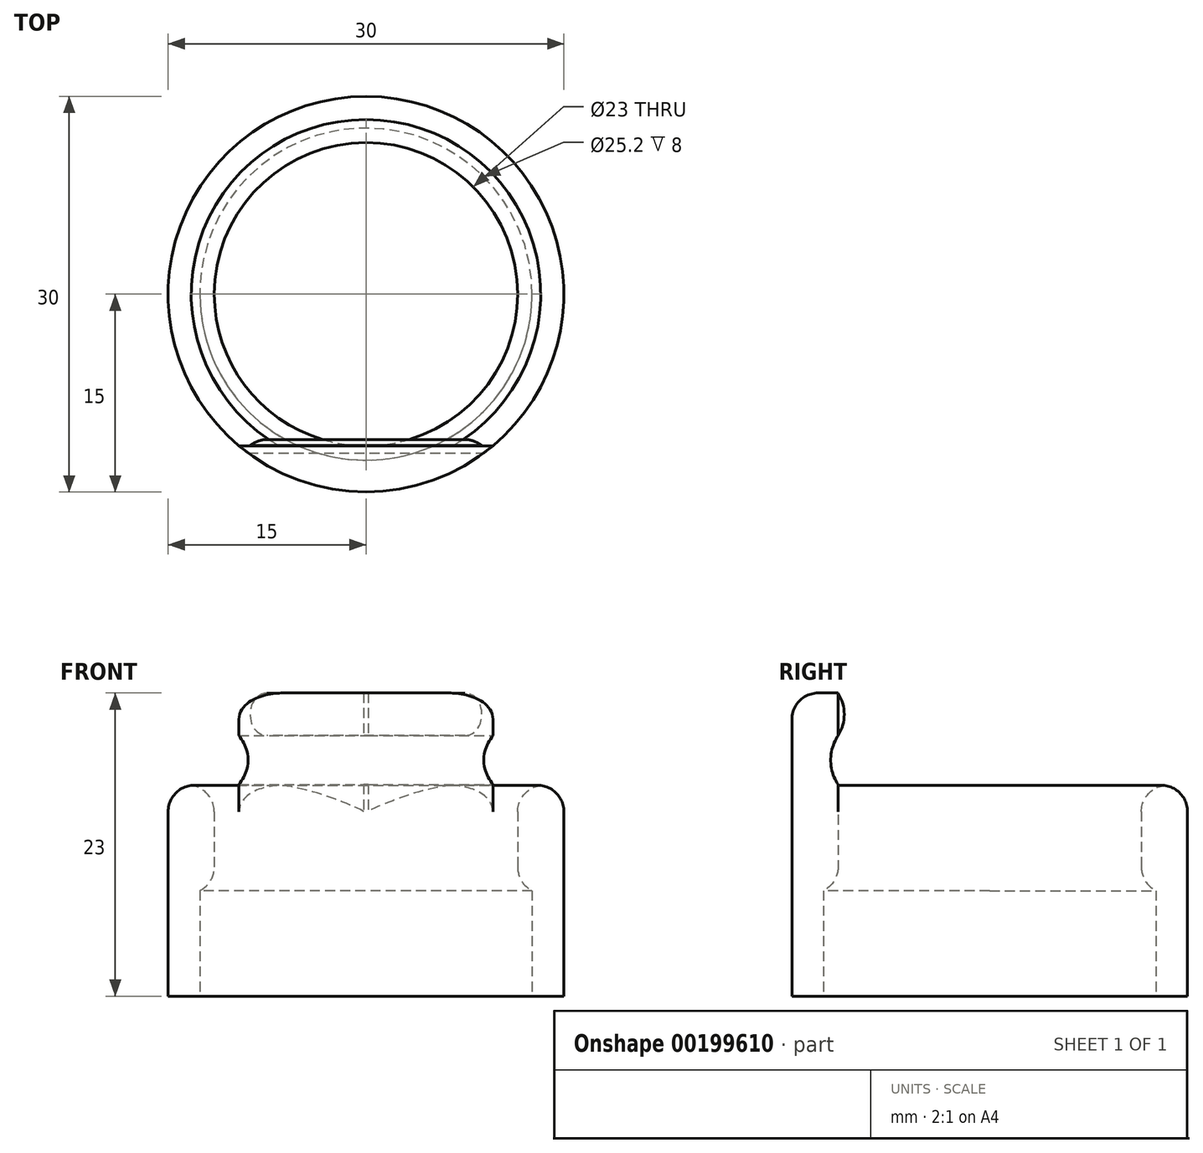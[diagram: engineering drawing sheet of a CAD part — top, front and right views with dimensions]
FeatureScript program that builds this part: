
annotation { "Feature Type Name" : "Feature", "Feature Type Description" : "" }
export const myFeature = defineFeature(function(context is Context, id is Id, definition is map)
    precondition{}
    {
        {
            var Q0;
            Q0=qCreatedBy(makeId("Top.planeOp"),FACE);
            var sketch = newSketch(context, id + "F0", { "sketchPlane" : qUnion([Q0])});
            skCircle(sketch, "E0", {"center": v(0, 0) * mm, "radius": 15 * mm});
            skCircle(sketch, "E1", {"center": v(0, 0) * mm, "radius": 12.6 * mm});
            skCircle(sketch, "E2", {"center": v(0, 0) * mm, "radius": 11.5 * mm});
            skLineSegment(sketch, "E3", {"start": v(0, -11.5) * mm, "end": v(9.63, -11.5) * mm});
            skLineSegment(sketch, "E4.MirrorCS", {"start": v(0, -11.5) * mm, "end": v(-9.63, -11.5) * mm});
            skSolve(sketch);
        }
        {
            var Q0;
            {var subQ0=sQuery(id+"F0.wireOp",EDGE,"E3");var subQ1=sQuery(id+"F0.wireOp",EDGE,"E0");var subQ2=makeQuery(id+"F0.imprint","INTERSECT",VERTEX,{"derivedFrom":[subQ1,subQ0]});Q0=makeQuery(id+"F0.imprint","IMPRINT",FACE,{"disambiguationData":[TD([[makeQuery(id+"F0.imprint","IMPRINT",EDGE,{"disambiguationData":[TD([[subQ2,-1.0]])],"derivedFrom":subQ1}),1.0]])]});}
            var Q1;
            {var subQ0=sQuery(id+"F0.wireOp",EDGE,"E3");var subQ1=sQuery(id+"F0.wireOp",EDGE,"E0");var subQ2=makeQuery(id+"F0.imprint","INTERSECT",VERTEX,{"derivedFrom":[subQ1,subQ0]});Q1=makeQuery(id+"F0.imprint","IMPRINT",FACE,{"disambiguationData":[TD([[makeQuery(id+"F0.imprint","IMPRINT",EDGE,{"disambiguationData":[TD([[subQ2,1.0]])],"derivedFrom":subQ1}),1.0]])]});}
            extrude(context, id + "F1", {"entities" : qUnion([Q0, Q1]), "endBound" : BoundingType.SYMMETRIC, "depth" : 16 * mm});
        }
        {
            var Q0;
            Q0 = qSketchRegion(id + "F0", true);
            var Q1;
            {var subQ5=sQuery(id+"F0.wireOp",EDGE,"E2");Q1=makeQuery(id+"F0.imprint","IMPRINT",FACE,{"disambiguationData":[TD([[makeQuery(id+"F0.imprint","IMPRINT",EDGE,{"derivedFrom":subQ5}),-1.0]])]});}
            var Q2;
            {var subQ0=sQuery(id+"F0.wireOp",EDGE,"E3");var subQ1=sQuery(id+"F0.wireOp",EDGE,"E1");var subQ2=makeQuery(id+"F0.imprint","INTERSECT",VERTEX,{"derivedFrom":[subQ1,subQ0]});Q2=makeQuery(id+"F0.imprint","IMPRINT",FACE,{"disambiguationData":[TD([[makeQuery(id+"F0.imprint","IMPRINT",EDGE,{"disambiguationData":[TD([[subQ2,1.0]])],"derivedFrom":subQ1}),1.0]])]});}
            extrude(context, id + "F2", {"entities" : qUnion([Q0, Q1, Q2]), "operationType" : NewBodyOperationType.ADD, "depth" : 8 * mm});
        }
        {
            var Q0;
            {var subQ0=sQuery(id+"F0.wireOp",EDGE,"E0");Q0=makeQuery(id+"F2.boolean.opBoolean","MERGE",FACE,{"derivedFrom":[makeQuery(id+"F1.opExtrude","CAP_FACE",FACE,{"disambiguationData":[OSD([subQ0,sQuery(id+"F0.wireOp",EDGE,"E1")])],"isStart":false}),makeQuery(id+"F2.opExtrude","CAP_FACE",FACE,{"disambiguationData":[OSD([subQ0,sQuery(id+"F0.wireOp",EDGE,"E2")])],"isStart":false})]});}
            var sketch = newSketch(context, id + "F3", { "sketchPlane" : qUnion([Q0])});
            skLineSegment(sketch, "E5", {"start": v(-9.63, -11.5) * mm, "end": v(9.63, -11.5) * mm});
            skArc(sketch, "E6", {"start": v(-9.63, -11.5) * mm, "mid": v(0, -15) * mm, "end": v(9.63, -11.5) * mm});
            skSolve(sketch);
        }
        {
            var Q0;
            {var subQ0=sQuery(id+"F3.wireOp",EDGE,"E6");Q0=makeQuery(id+"F3.imprint","IMPRINT",FACE,{"disambiguationData":[TD([[makeQuery(id+"F3.imprint","IMPRINT",EDGE,{"derivedFrom":subQ0}),1.0]])]});}
            extrude(context, id + "F4", {"entities" : qUnion([Q0]), "operationType" : NewBodyOperationType.ADD, "depth" : 7 * mm});
        }
        {
            var Q0;
            Q0=qCreatedBy(makeId("Right.planeOp"),FACE);
            var sketch = newSketch(context, id + "F5", { "sketchPlane" : qUnion([Q0])});
            skArc(sketch, "E7", {"start": v(-11.5, 11.77) * mm, "mid": v(-12.05, 9.9) * mm, "end": v(-11.48, 8.02) * mm});
            skArc(sketch, "E8", {"start": v(-11.5, 11.77) * mm, "mid": v(-11.03, 13.38) * mm, "end": v(-11.5, 14.99) * mm});
            skLineSegment(sketch, "E9", {"start": v(-11.48, 8.02) * mm, "end": v(-11.5, 11.77) * mm});
            skLineSegment(sketch, "E10", {"start": v(-11.5, 11.77) * mm, "end": v(-11.5, 14.99) * mm});
            skSolve(sketch);
        }
        {
            var Q0;
            Q0=makeQuery(id+"F5.imprint","IMPRINT",FACE,{"disambiguationData":[TD([[makeQuery(id+"F5.imprint","IMPRINT",EDGE,{"derivedFrom":sQuery(id+"F5.wireOp",EDGE,"E7")}),1.0]])]});
            extrude(context, id + "F6", {"entities" : qUnion([Q0]), "operationType" : NewBodyOperationType.REMOVE, "endBound" : BoundingType.SYMMETRIC, "oppositeDirection" : true, "depth" : 25 * mm});
        }
        {
            var Q0;
            Q0=makeQuery(id+"F2.opExtrude","CAP_EDGE",EDGE,{"disambiguationData":[OSD([sQuery(id+"F0.wireOp",EDGE,"E2")])],"isStart":false});
            var Q1;
            Q1=makeQuery(id+"F2.opExtrude","CAP_EDGE",EDGE,{"disambiguationData":[OSD([sQuery(id+"F0.wireOp",EDGE,"E2")])],"isStart":true});
            var Q2;
            Q2=makeQuery(id+"F4.boolean.opBoolean","SPLIT",EDGE,{"derivedFrom":makeQuery(id+"F1.opExtrude","CAP_EDGE",EDGE,{"disambiguationData":[OSD([sQuery(id+"F0.wireOp",EDGE,"E0")])],"isStart":false})});
            var Q3;
            Q3=makeQuery(id+"F4.opExtrude","CAP_EDGE",EDGE,{"disambiguationData":[OSD([sQuery(id+"F3.wireOp",EDGE,"E6")])],"isStart":false});
            fillet(context, id + "F7", {"entities" : qUnion([Q0, Q1, Q2, Q3]), "radius" : 2 * mm, "tangentPropagation" : true, "allowEdgeOverflow" : false});
        }
        {
            var Q0;
            Q0=makeQuery(id+"F5.imprint","IMPRINT",FACE,{"disambiguationData":[TD([[makeQuery(id+"F5.imprint","IMPRINT",EDGE,{"derivedFrom":sQuery(id+"F5.wireOp",EDGE,"E8")}),1.0]])]});
            extrude(context, id + "F8", {"entities" : qUnion([Q0]), "operationType" : NewBodyOperationType.ADD, "endBound" : BoundingType.SYMMETRIC, "depth" : 19 * mm});
        }
        {
            var Q0;
            Q0=makeQuery(id+"F8.opExtrude","CAP_EDGE",EDGE,{"disambiguationData":[OSD([sQuery(id+"F5.wireOp",EDGE,"E8")])],"isStart":false});
            var Q1;
            Q1=makeQuery(id+"F8.opExtrude","CAP_EDGE",EDGE,{"disambiguationData":[OSD([sQuery(id+"F5.wireOp",EDGE,"E8")])],"isStart":true});
            fillet(context, id + "F9", {"entities" : qUnion([Q0, Q1]), "radius" : 2 * mm, "tangentPropagation" : true, "allowEdgeOverflow" : false});
        }
    });
